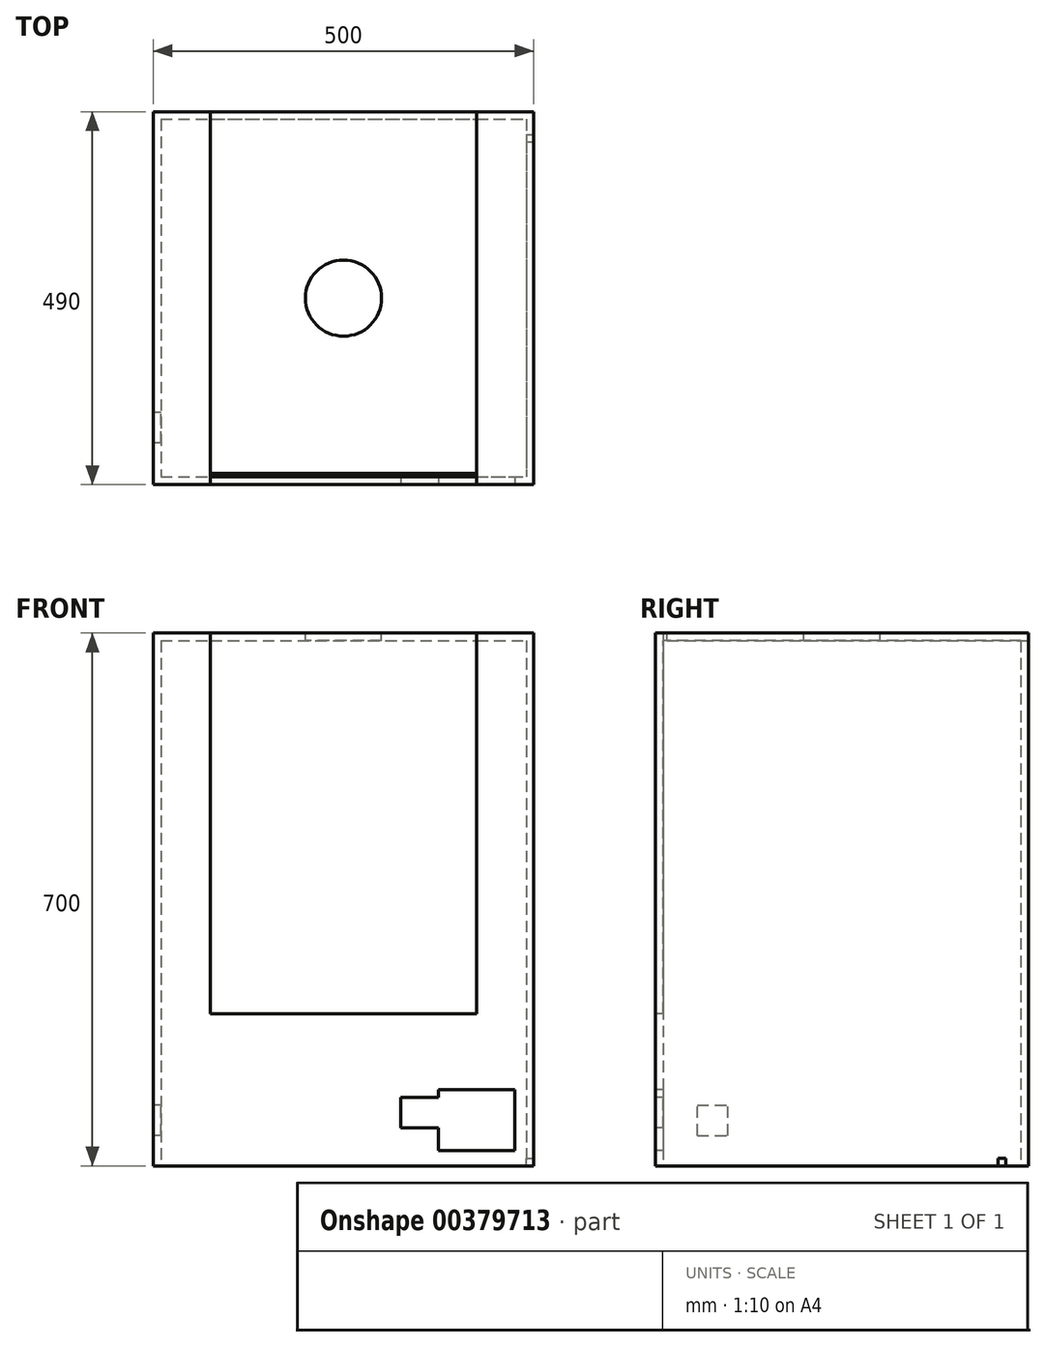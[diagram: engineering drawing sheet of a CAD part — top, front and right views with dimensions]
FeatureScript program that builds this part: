
annotation { "Feature Type Name" : "Feature", "Feature Type Description" : "" }
export const myFeature = defineFeature(function(context is Context, id is Id, definition is map)
    precondition{}
    {
        {
            var Q0;
            Q0=qCreatedBy(makeId("Top.planeOp"),FACE);
            var sketch = newSketch(context, id + "F0", { "sketchPlane" : qUnion([Q0])});
            skLineSegment(sketch, "E0.bottom", {"start": v(-137.12, 349.13) * mm, "end": v(362.88, 349.13) * mm});
            skLineSegment(sketch, "E0.top", {"start": v(-137.12, -140.87) * mm, "end": v(362.88, -140.87) * mm});
            skLineSegment(sketch, "E0.left", {"start": v(-137.12, 349.13) * mm, "end": v(-137.12, -140.87) * mm});
            skLineSegment(sketch, "E0.right", {"start": v(362.88, 349.13) * mm, "end": v(362.88, -140.87) * mm});
            skLineSegment(sketch, "E1.bottom", {"start": v(-127.12, 339.13) * mm, "end": v(352.88, 339.13) * mm});
            skLineSegment(sketch, "E1.top", {"start": v(-127.12, -130.87) * mm, "end": v(352.88, -130.87) * mm});
            skLineSegment(sketch, "E1.left", {"start": v(-127.12, 339.13) * mm, "end": v(-127.12, -130.87) * mm});
            skLineSegment(sketch, "E1.right", {"start": v(352.88, 339.13) * mm, "end": v(352.88, -130.87) * mm});
            skSolve(sketch);
        }
        {
            var Q0;
            Q0=makeQuery(id+"F0.imprint","IMPRINT",FACE,{"disambiguationData":[TD([[makeQuery(id+"F0.imprint","IMPRINT",EDGE,{"derivedFrom":sQuery(id+"F0.wireOp",EDGE,"E0.bottom")}),-1.0]])]});
            extrude(context, id + "F1", {"entities" : qUnion([Q0]), "depth" : 700 * mm});
        }
        {
            var Q0;
            Q0=makeQuery(id+"F1.opExtrude","CAP_FACE",FACE,{"disambiguationData":[OSD([sQuery(id+"F0.wireOp",EDGE,"E0.bottom"),sQuery(id+"F0.wireOp",EDGE,"E0.top"),sQuery(id+"F0.wireOp",EDGE,"E0.left"),sQuery(id+"F0.wireOp",EDGE,"E0.right"),sQuery(id+"F0.wireOp",EDGE,"E1.bottom"),sQuery(id+"F0.wireOp",EDGE,"E1.top"),sQuery(id+"F0.wireOp",EDGE,"E1.left"),sQuery(id+"F0.wireOp",EDGE,"E1.right")])],"isStart":false});
            var sketch = newSketch(context, id + "F2", { "sketchPlane" : qUnion([Q0])});
            skLineSegment(sketch, "E2.bottom", {"start": v(352.88, 339.13) * mm, "end": v(-127.12, 339.13) * mm});
            skLineSegment(sketch, "E2.top", {"start": v(352.88, -130.87) * mm, "end": v(-127.12, -130.87) * mm});
            skLineSegment(sketch, "E2.left", {"start": v(352.88, 339.13) * mm, "end": v(352.88, -130.87) * mm});
            skLineSegment(sketch, "E2.right", {"start": v(-127.12, 339.13) * mm, "end": v(-127.12, -130.87) * mm});
            skSolve(sketch);
        }
        {
            var Q0;
            Q0=makeQuery(id+"F2.imprint","IMPRINT",FACE,{"disambiguationData":[TD([[makeQuery(id+"F2.imprint","IMPRINT",EDGE,{"derivedFrom":sQuery(id+"F2.wireOp",EDGE,"E2.bottom")}),-1.0]])]});
            extrude(context, id + "F3", {"entities" : qUnion([Q0]), "operationType" : NewBodyOperationType.ADD, "oppositeDirection" : true, "depth" : 10 * mm});
        }
        {
            var Q0;
            Q0=makeQuery(id+"F1.opExtrude","SWEPT_FACE",FACE,{"disambiguationData":[OSD([sQuery(id+"F0.wireOp",EDGE,"E0.top")])]});
            var sketch = newSketch(context, id + "F4", { "sketchPlane" : qUnion([Q0])});
            skLineSegment(sketch, "E3.bottom", {"start": v(337.88, 20) * mm, "end": v(237.88, 20) * mm});
            skLineSegment(sketch, "E3.top", {"start": v(337.88, 100) * mm, "end": v(237.88, 100) * mm});
            skLineSegment(sketch, "E3.left", {"start": v(337.88, 20) * mm, "end": v(337.88, 100) * mm});
            skLineSegment(sketch, "E3.right", {"start": v(237.88, 20) * mm, "end": v(237.88, 100) * mm});
            skLineSegment(sketch, "E4.bottom", {"start": v(187.88, 90) * mm, "end": v(237.88, 90) * mm});
            skLineSegment(sketch, "E4.top", {"start": v(187.88, 50) * mm, "end": v(237.88, 50) * mm});
            skLineSegment(sketch, "E4.left", {"start": v(187.88, 90) * mm, "end": v(187.88, 50) * mm});
            skLineSegment(sketch, "E4.right", {"start": v(237.88, 90) * mm, "end": v(237.88, 50) * mm});
            skSolve(sketch);
        }
        {
            var Q0;
            {var subQ1=sQuery(id+"F4.wireOp",EDGE,"E3.bottom");Q0=makeQuery(id+"F4.imprint","IMPRINT",FACE,{"disambiguationData":[TD([[makeQuery(id+"F4.imprint","IMPRINT",EDGE,{"derivedFrom":subQ1}),-1.0]])]});}
            var Q1;
            Q1=makeQuery(id+"F4.imprint","IMPRINT",FACE,{"disambiguationData":[TD([[makeQuery(id+"F4.imprint","IMPRINT",EDGE,{"derivedFrom":sQuery(id+"F4.wireOp",EDGE,"E4.bottom")}),-1.0]])]});
            extrude(context, id + "F5", {"entities" : qUnion([Q0, Q1]), "operationType" : NewBodyOperationType.REMOVE, "oppositeDirection" : true, "depth" : 25 * mm});
        }
        {
            var Q0;
            Q0=makeQuery(id+"F1.opExtrude","SWEPT_FACE",FACE,{"disambiguationData":[OSD([sQuery(id+"F0.wireOp",EDGE,"E0.left")])]});
            var sketch = newSketch(context, id + "F6", { "sketchPlane" : qUnion([Q0])});
            skLineSegment(sketch, "E5.bottom", {"start": v(45.87, 80) * mm, "end": v(85.87, 80) * mm});
            skLineSegment(sketch, "E5.top", {"start": v(45.87, 40) * mm, "end": v(85.87, 40) * mm});
            skLineSegment(sketch, "E5.left", {"start": v(45.87, 80) * mm, "end": v(45.87, 40) * mm});
            skLineSegment(sketch, "E5.right", {"start": v(85.87, 80) * mm, "end": v(85.87, 40) * mm});
            skSolve(sketch);
        }
        {
            var Q0;
            Q0=makeQuery(id+"F6.imprint","IMPRINT",FACE,{"disambiguationData":[TD([[makeQuery(id+"F6.imprint","IMPRINT",EDGE,{"derivedFrom":sQuery(id+"F6.wireOp",EDGE,"E5.bottom")}),-1.0]])]});
            extrude(context, id + "F7", {"entities" : qUnion([Q0]), "operationType" : NewBodyOperationType.REMOVE, "oppositeDirection" : true, "depth" : 25 * mm});
        }
        {
            var Q0;
            Q0=makeQuery(id+"F1.opExtrude","SWEPT_FACE",FACE,{"disambiguationData":[OSD([sQuery(id+"F0.wireOp",EDGE,"E0.right")])]});
            var sketch = newSketch(context, id + "F8", { "sketchPlane" : qUnion([Q0])});
            skLineSegment(sketch, "E6.bottom", {"start": v(319.13, 0) * mm, "end": v(309.13, 0) * mm});
            skLineSegment(sketch, "E6.top", {"start": v(319.13, 10) * mm, "end": v(309.13, 10) * mm});
            skLineSegment(sketch, "E6.left", {"start": v(319.13, 0) * mm, "end": v(319.13, 10) * mm});
            skLineSegment(sketch, "E6.right", {"start": v(309.13, 0) * mm, "end": v(309.13, 10) * mm});
            skSolve(sketch);
        }
        {
            var Q0;
            Q0=makeQuery(id+"F8.imprint","IMPRINT",FACE,{"disambiguationData":[TD([[makeQuery(id+"F8.imprint","IMPRINT",EDGE,{"derivedFrom":sQuery(id+"F8.wireOp",EDGE,"E6.bottom")}),-1.0]])]});
            extrude(context, id + "F9", {"entities" : qUnion([Q0]), "operationType" : NewBodyOperationType.REMOVE, "oppositeDirection" : true, "depth" : 25 * mm});
        }
        {
            var Q0;
            Q0=makeQuery(id+"F1.opExtrude","SWEPT_FACE",FACE,{"disambiguationData":[OSD([sQuery(id+"F0.wireOp",EDGE,"E0.top")])]});
            var sketch = newSketch(context, id + "F10", { "sketchPlane" : qUnion([Q0])});
            skLineSegment(sketch, "E7.bottom", {"start": v(-62.12, 700) * mm, "end": v(287.88, 700) * mm});
            skLineSegment(sketch, "E7.top", {"start": v(-62.12, 200) * mm, "end": v(287.88, 200) * mm});
            skLineSegment(sketch, "E7.left", {"start": v(-62.12, 700) * mm, "end": v(-62.12, 200) * mm});
            skLineSegment(sketch, "E7.right", {"start": v(287.88, 700) * mm, "end": v(287.88, 200) * mm});
            skSolve(sketch);
        }
        {
            var Q0;
            Q0=makeQuery(id+"F10.imprint","IMPRINT",FACE,{"disambiguationData":[TD([[makeQuery(id+"F10.imprint","IMPRINT",EDGE,{"derivedFrom":sQuery(id+"F10.wireOp",EDGE,"E7.bottom")}),-1.0]])]});
            extrude(context, id + "F11", {"entities" : qUnion([Q0]), "operationType" : NewBodyOperationType.REMOVE, "oppositeDirection" : true, "depth" : 15 * mm});
        }
        {
            var Q0;
            Q0 = qSketchRegion(id + "F10", true);
            extrude(context, id + "F12", {"entities" : qUnion([Q0]), "oppositeDirection" : true, "depth" : 10 * mm});
        }
        {
            var Q0;
            Q0=makeQuery(id+"F3.boolean.opBoolean","MERGE",FACE,{"derivedFrom":[makeQuery(id+"F1.opExtrude","CAP_FACE",FACE,{"disambiguationData":[OSD([sQuery(id+"F0.wireOp",EDGE,"E0.bottom"),sQuery(id+"F0.wireOp",EDGE,"E0.top"),sQuery(id+"F0.wireOp",EDGE,"E0.left"),sQuery(id+"F0.wireOp",EDGE,"E0.right"),sQuery(id+"F0.wireOp",EDGE,"E1.bottom"),sQuery(id+"F0.wireOp",EDGE,"E1.top"),sQuery(id+"F0.wireOp",EDGE,"E1.left"),sQuery(id+"F0.wireOp",EDGE,"E1.right")])],"isStart":false}),makeQuery(id+"F3.opExtrude","CAP_FACE",FACE,{"disambiguationData":[OSD([sQuery(id+"F2.wireOp",EDGE,"E2.bottom"),sQuery(id+"F2.wireOp",EDGE,"E2.top"),sQuery(id+"F2.wireOp",EDGE,"E2.left"),sQuery(id+"F2.wireOp",EDGE,"E2.right")])],"isStart":true})]});
            var sketch = newSketch(context, id + "F13", { "sketchPlane" : qUnion([Q0])});
            skLineSegment(sketch, "E8.bottom", {"start": v(-62.12, -125.87) * mm, "end": v(287.88, -125.87) * mm});
            skLineSegment(sketch, "E8.top", {"start": v(-62.12, 349.13) * mm, "end": v(287.88, 349.13) * mm});
            skLineSegment(sketch, "E8.left", {"start": v(-62.12, -125.87) * mm, "end": v(-62.12, 349.13) * mm});
            skLineSegment(sketch, "E8.right", {"start": v(287.88, -125.87) * mm, "end": v(287.88, 349.13) * mm});
            skSolve(sketch);
        }
        {
            var Q0;
            Q0=makeQuery(id+"F13.imprint","IMPRINT",FACE,{"disambiguationData":[TD([[makeQuery(id+"F13.imprint","IMPRINT",EDGE,{"derivedFrom":sQuery(id+"F13.wireOp",EDGE,"E8.bottom")}),1.0]])]});
            extrude(context, id + "F14", {"entities" : qUnion([Q0]), "operationType" : NewBodyOperationType.REMOVE, "oppositeDirection" : true, "depth" : 10 * mm});
        }
        {
            var Q0;
            Q0 = qSketchRegion(id + "F13", true);
            extrude(context, id + "F15", {"entities" : qUnion([Q0]), "oppositeDirection" : true, "depth" : 10 * mm});
        }
        {
            var Q0;
            Q0=makeQuery(id+"F15.opExtrude","CAP_FACE",FACE,{"disambiguationData":[OSD([sQuery(id+"F13.wireOp",EDGE,"E8.bottom"),sQuery(id+"F13.wireOp",EDGE,"E8.top"),sQuery(id+"F13.wireOp",EDGE,"E8.left"),sQuery(id+"F13.wireOp",EDGE,"E8.right")])],"isStart":true});
            var sketch = newSketch(context, id + "F16", { "sketchPlane" : qUnion([Q0])});
            skCircle(sketch, "E9", {"center": v(112.88, 104.13) * mm, "radius": 50 * mm});
            skSolve(sketch);
        }
        {
            var Q0;
            Q0=makeQuery(id+"F16.imprint","IMPRINT",FACE,{"disambiguationData":[TD([[makeQuery(id+"F16.imprint","IMPRINT",EDGE,{"derivedFrom":sQuery(id+"F16.wireOp",EDGE,"E9")}),1.0]])]});
            extrude(context, id + "F17", {"entities" : qUnion([Q0]), "operationType" : NewBodyOperationType.REMOVE, "oppositeDirection" : true, "depth" : 10 * mm});
        }
    });
